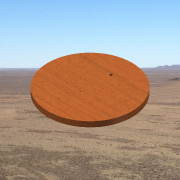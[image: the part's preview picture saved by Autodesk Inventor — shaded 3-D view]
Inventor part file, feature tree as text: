
AUTODESK INVENTOR PART (.ipt)
format: ipt  version: 2014 SP1 (Build 180222100, 222)  size: 132,608 bytes
history: native  units: in
note: dims shown in document units (in); Inventor stores cm internally (conversion verified against a paired STEP export)
features: sketch x2, extrude x1, hole x1
ambient origin geometry x8: Origin, YZ Plane, XZ Plane, XY Plane, X Axis, Y Axis, Z Axis, Center Point
bodies: Solid1 (feature_tree)
feature tree (4):
  extrude  "Extrusion1"  Depth=0.5in TaperAngle=0.0deg
  hole  "Hole1"  [1 undecoded]
  sketch  "Sketch1"  dims[d0=8.0in d1=0.5in d2=0.0in]
  sketch  "Sketch2"  dims[d3=0.25in d4=0.75in d5=0.375in d6=0.25in d7=0.5635in d8=1.0in d9=0.8108in]
note: 1 required parameter value undecoded (feature->parameter linkage not recoverable at this tier; creation-order binding heuristic only, values carry confidence <= 0.55)
